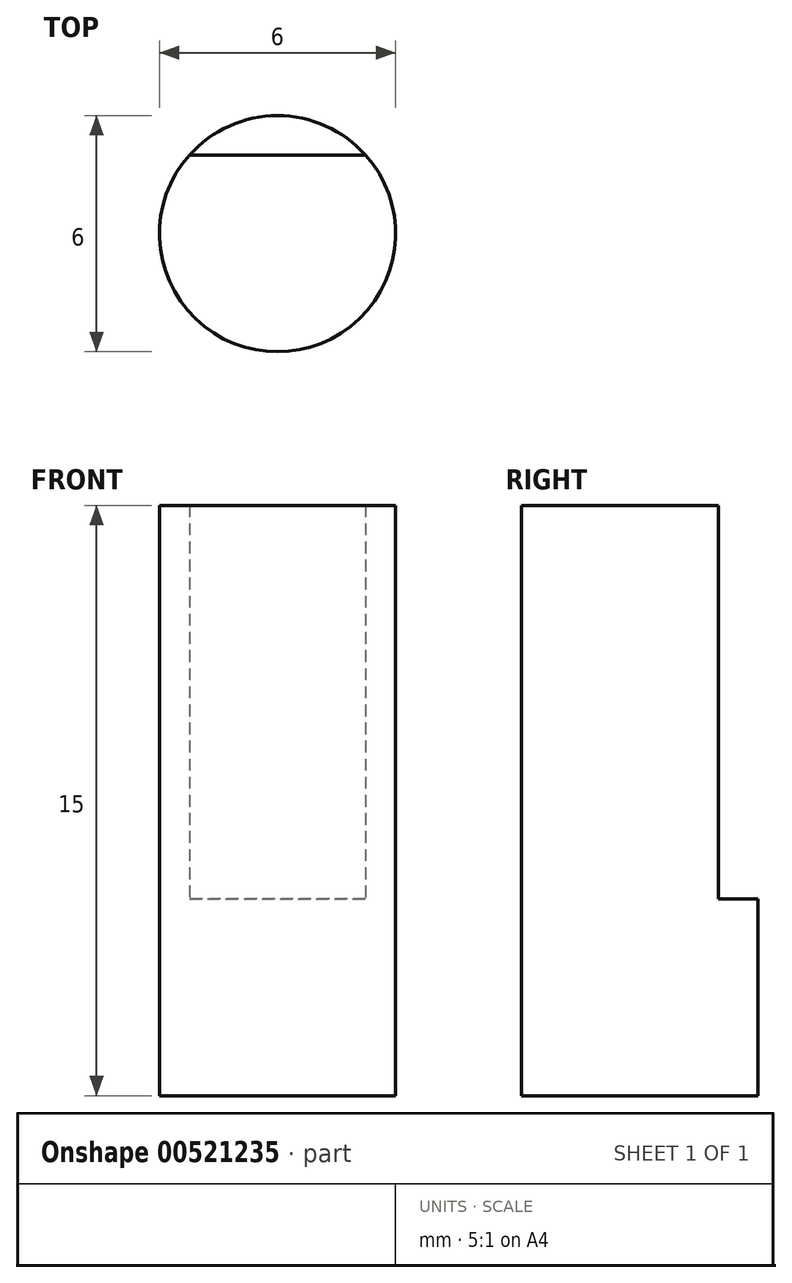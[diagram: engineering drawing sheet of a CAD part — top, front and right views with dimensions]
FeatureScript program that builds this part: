
annotation { "Feature Type Name" : "Feature", "Feature Type Description" : "" }
export const myFeature = defineFeature(function(context is Context, id is Id, definition is map)
    precondition{}
    {
        {
            var Q0;
            Q0=qCreatedBy(makeId("Top.planeOp"),FACE);
            var sketch = newSketch(context, id + "F0", { "sketchPlane" : qUnion([Q0])});
            skCircle(sketch, "E0", {"center": v(0, 0) * mm, "radius": 3 * mm});
            skSolve(sketch);
        }
        {
            var Q0;
            Q0 = qSketchRegion(id + "F0", true);
            extrude(context, id + "F1", {"entities" : qUnion([Q0]), "depth" : 15 * mm, "offsetDistance" : 25.4 * mm});
        }
        {
            var Q0;
            Q0=makeQuery(id+"F1.opExtrude","CAP_FACE",FACE,{"disambiguationData":[OSD([sQuery(id+"F0.wireOp",EDGE,"E0")])],"isStart":false});
            var sketch = newSketch(context, id + "F2", { "sketchPlane" : qUnion([Q0])});
            skLineSegment(sketch, "E1.bottom", {"start": v(0, 3) * mm, "end": v(3.7, 3) * mm});
            skLineSegment(sketch, "E1.top", {"start": v(0, 2) * mm, "end": v(3.7, 2) * mm});
            skLineSegment(sketch, "E1.right", {"start": v(3.7, 3) * mm, "end": v(3.7, 2) * mm});
            skLineSegment(sketch, "E2.MirrorCS", {"start": v(0, 3) * mm, "end": v(-3.7, 3) * mm});
            skLineSegment(sketch, "E3.MirrorCS", {"start": v(0, 2) * mm, "end": v(-3.7, 2) * mm});
            skLineSegment(sketch, "E4.MirrorCS", {"start": v(-3.7, 3) * mm, "end": v(-3.7, 2) * mm});
            skSolve(sketch);
        }
        {
            var Q0;
            Q0 = qSketchRegion(id + "F2", true);
            extrude(context, id + "F3", {"entities" : qUnion([Q0]), "operationType" : NewBodyOperationType.REMOVE, "oppositeDirection" : true, "depth" : 10 * mm, "offsetDistance" : 25.4 * mm});
        }
    });
